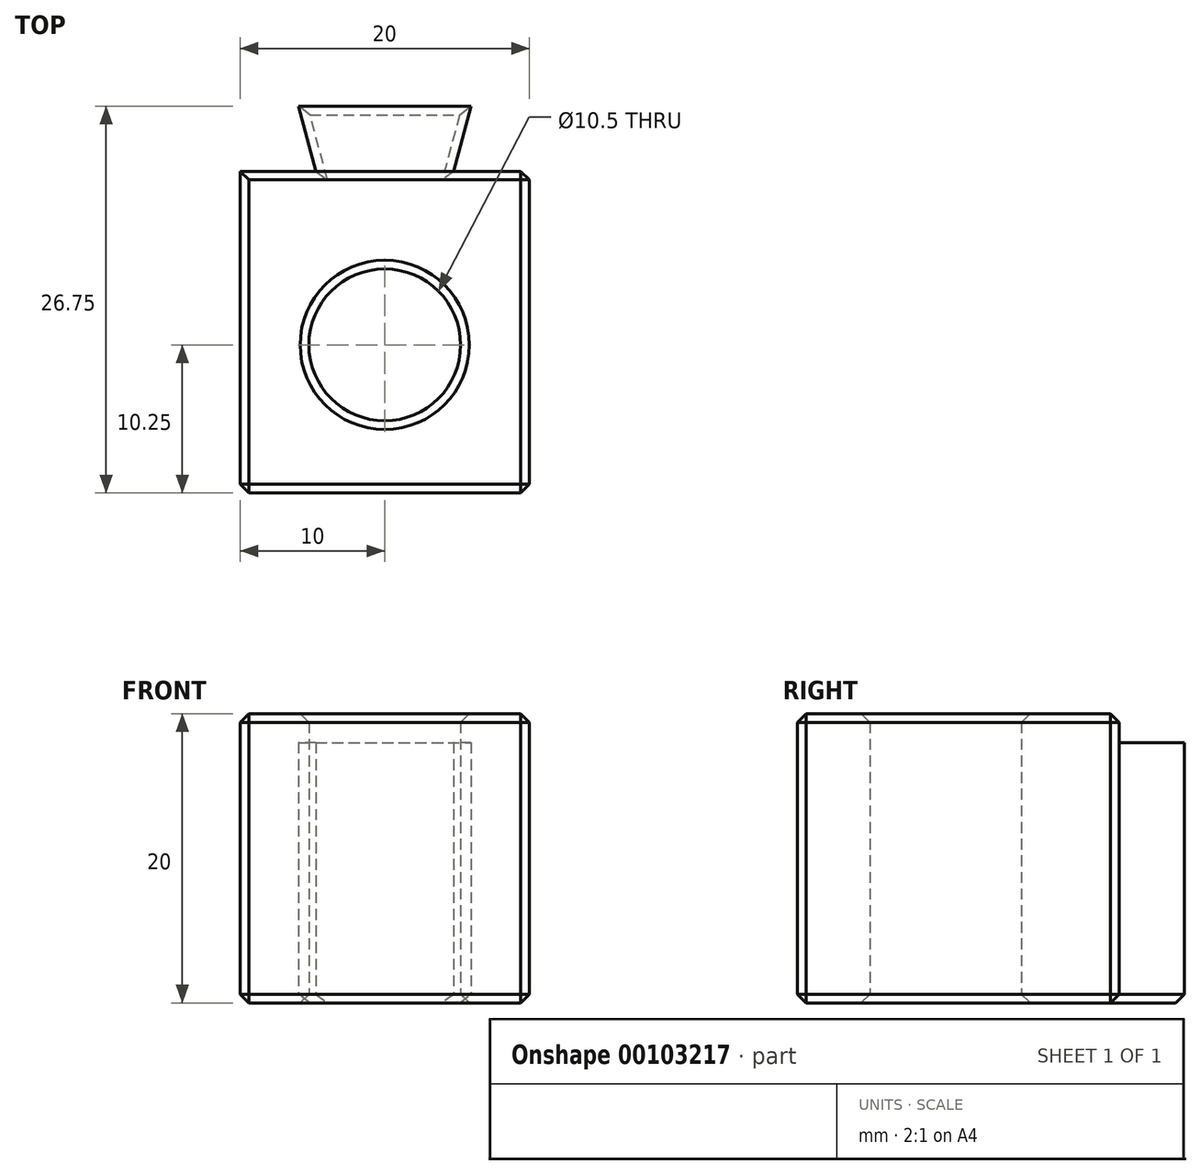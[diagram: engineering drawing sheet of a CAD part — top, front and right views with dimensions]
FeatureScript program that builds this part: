
annotation { "Feature Type Name" : "Feature", "Feature Type Description" : "" }
export const myFeature = defineFeature(function(context is Context, id is Id, definition is map)
    precondition{}
    {
        {
            assignVariable(context, id + "F0", {"name" : "ClampThickness", "anyValue" : 20});
        }
        {
            assignVariable(context, id + "F1", {"name" : "DovetailBackstopDepth", "anyValue" : 2});
        }
        {
            var Q0;
            Q0=qCreatedBy(makeId("Top.planeOp"),FACE);
            var sketch = newSketch(context, id + "F2", { "sketchPlane" : qUnion([Q0])});
            skLineSegment(sketch, "E0", {"start": v(0, 22.25) * mm, "end": v(5.25, 22.25) * mm});
            skLineSegment(sketch, "E1", {"start": v(5.25, 22.25) * mm, "end": v(4.04, 26.75) * mm});
            skLineSegment(sketch, "E2", {"start": v(4.04, 26.75) * mm, "end": v(15.96, 26.75) * mm});
            skLineSegment(sketch, "E3", {"start": v(15.96, 26.75) * mm, "end": v(14.75, 22.25) * mm});
            skLineSegment(sketch, "E4", {"start": v(14.75, 22.25) * mm, "end": v(20, 22.25) * mm});
            skLineSegment(sketch, "E5", {"start": v(0, 22.25) * mm, "end": v(0, 0) * mm});
            skLineSegment(sketch, "E6", {"start": v(0, 0) * mm, "end": v(20, 0) * mm});
            skLineSegment(sketch, "E7", {"start": v(20, 0) * mm, "end": v(20, 22.25) * mm});
            skLineSegment(sketch, "E8", {"start": v(10, 0) * mm, "end": v(10, 26.75) * mm, "construction": true});
            skCircle(sketch, "E9", {"center": v(10, 10.25) * mm, "radius": 5.25 * mm});
            skLineSegment(sketch, "E10", {"start": v(5.25, 22.25) * mm, "end": v(14.75, 22.25) * mm});
            skSolve(sketch);
        }
        {
            var Q0;
            {var subQ3=sQuery(id+"F2.wireOp",EDGE,"E0");Q0=makeQuery(id+"F2.imprint","IMPRINT",FACE,{"disambiguationData":[TD([[makeQuery(id+"F2.imprint","IMPRINT",EDGE,{"derivedFrom":subQ3}),-1.0]])]});}
            var Q1;
            {var subQ0=sQuery(id+"F2.wireOp",EDGE,"VYWeHY0D-dY77-4kFr-xTyd-c2evzxD8G3UU");Q1=makeQuery(id+"F2.imprint","IMPRINT",FACE,{"disambiguationData":[TD([[makeQuery(id+"F2.imprint","IMPRINT",EDGE,{"derivedFrom":subQ0}),-1.0]])]});}
            var Q2;
            {var subQ0=sQuery(id+"F2.wireOp",EDGE,"xa0Oe4SL-IEjK-Ohqs-II2J-3vTqthCB0wox");Q2=makeQuery(id+"F2.imprint","IMPRINT",FACE,{"disambiguationData":[TD([[makeQuery(id+"F2.imprint","IMPRINT",EDGE,{"derivedFrom":subQ0}),-1.0]])]});}
            extrude(context, id + "F3", {"entities" : qUnion([Q0, Q1, Q2]), "depth" : (getVariable(context, 'ClampThickness')) * mm});
        }
        {
            var Q0;
            Q0=makeQuery(id+"F2.imprint","IMPRINT",FACE,{"disambiguationData":[TD([[makeQuery(id+"F2.imprint","IMPRINT",EDGE,{"derivedFrom":sQuery(id+"F2.wireOp",EDGE,"E1")}),-1.0]])]});
            extrude(context, id + "F4", {"entities" : qUnion([Q0]), "operationType" : NewBodyOperationType.ADD, "depth" : (getVariable(context, 'ClampThickness') - getVariable(context, 'DovetailBackstopDepth')) * mm});
        }
        {
            var Q0;
            {var subQ0=sQuery(id+"F2.wireOp",EDGE,"E10");var subQ1=sQuery(id+"F2.wireOp",EDGE,"98ce6dfb-64ee-43a4-b6a5-ae194eb404b20.MirrorCS");var subQ2=sQuery(id+"F2.wireOp",EDGE,"ohmSc0VC-r7ha-bODf-CrWD-XmSzwEfXU5ou");var subQ3=sQuery(id+"F2.wireOp",EDGE,"0MaYhBST-z4TI-CUlx-1Ce4-Bb947fno3LJP");var subQ4=sQuery(id+"F2.wireOp",EDGE,"E5");Q0=makeQuery(id+"F4.boolean.opBoolean","MERGE",FACE,{"derivedFrom":[makeQuery(id+"FvwmsusxJ3vFSSD_1.boolean.opBoolean","MERGE",FACE,{"derivedFrom":[makeQuery(id+"F3.opExtrude","CAP_FACE",FACE,{"disambiguationData":[OSD([sQuery(id+"F2.wireOp",EDGE,"E0"),sQuery(id+"F2.wireOp",EDGE,"E4"),subQ4,sQuery(id+"F2.wireOp",EDGE,"E6"),sQuery(id+"F2.wireOp",EDGE,"E7"),sQuery(id+"F2.wireOp",EDGE,"E9"),subQ0,sQuery(id+"F2.wireOp",EDGE,"xa0Oe4SL-IEjK-Ohqs-II2J-3vTqthCB0wox"),subQ3,sQuery(id+"F2.wireOp",EDGE,"VYWeHY0D-dY77-4kFr-xTyd-c2evzxD8G3UU"),subQ2,subQ1])],"isStart":true}),makeQuery(id+"FvwmsusxJ3vFSSD_1.opExtrude","CAP_FACE",FACE,{"disambiguationData":[OSD([subQ4,subQ3,subQ2,subQ1])],"isStart":true})]}),makeQuery(id+"F4.opExtrude","CAP_FACE",FACE,{"disambiguationData":[OSD([sQuery(id+"F2.wireOp",EDGE,"E1"),sQuery(id+"F2.wireOp",EDGE,"E2"),sQuery(id+"F2.wireOp",EDGE,"E3"),subQ0])],"isStart":true})]});}
            var Q1;
            Q1=makeQuery(id+"F3.opExtrude","CAP_FACE",FACE,{"disambiguationData":[OSD([sQuery(id+"F2.wireOp",EDGE,"E0"),sQuery(id+"F2.wireOp",EDGE,"E4"),sQuery(id+"F2.wireOp",EDGE,"E5"),sQuery(id+"F2.wireOp",EDGE,"E6"),sQuery(id+"F2.wireOp",EDGE,"E7"),sQuery(id+"F2.wireOp",EDGE,"E9"),sQuery(id+"F2.wireOp",EDGE,"E10"),sQuery(id+"F2.wireOp",EDGE,"xa0Oe4SL-IEjK-Ohqs-II2J-3vTqthCB0wox"),sQuery(id+"F2.wireOp",EDGE,"0MaYhBST-z4TI-CUlx-1Ce4-Bb947fno3LJP"),sQuery(id+"F2.wireOp",EDGE,"VYWeHY0D-dY77-4kFr-xTyd-c2evzxD8G3UU"),sQuery(id+"F2.wireOp",EDGE,"ohmSc0VC-r7ha-bODf-CrWD-XmSzwEfXU5ou"),sQuery(id+"F2.wireOp",EDGE,"98ce6dfb-64ee-43a4-b6a5-ae194eb404b20.MirrorCS")])],"isStart":false});
            var Q2;
            Q2=makeQuery(id+"F3.opExtrude","SWEPT_FACE",FACE,{"disambiguationData":[OSD([sQuery(id+"F2.wireOp",EDGE,"E6"),sQuery(id+"F2.wireOp",EDGE,"xa0Oe4SL-IEjK-Ohqs-II2J-3vTqthCB0wox")])]});
            var Q3;
            Q3=makeQuery(id+"F3.opExtrude","SWEPT_FACE",FACE,{"disambiguationData":[OSD([sQuery(id+"F2.wireOp",EDGE,"E7")])]});
            chamfer(context, id + "F5", {"entities" : qUnion([Q0, Q1, Q2, Q3]), "width" : 0.6 * mm, "tangentPropagation" : true});
        }
    });
